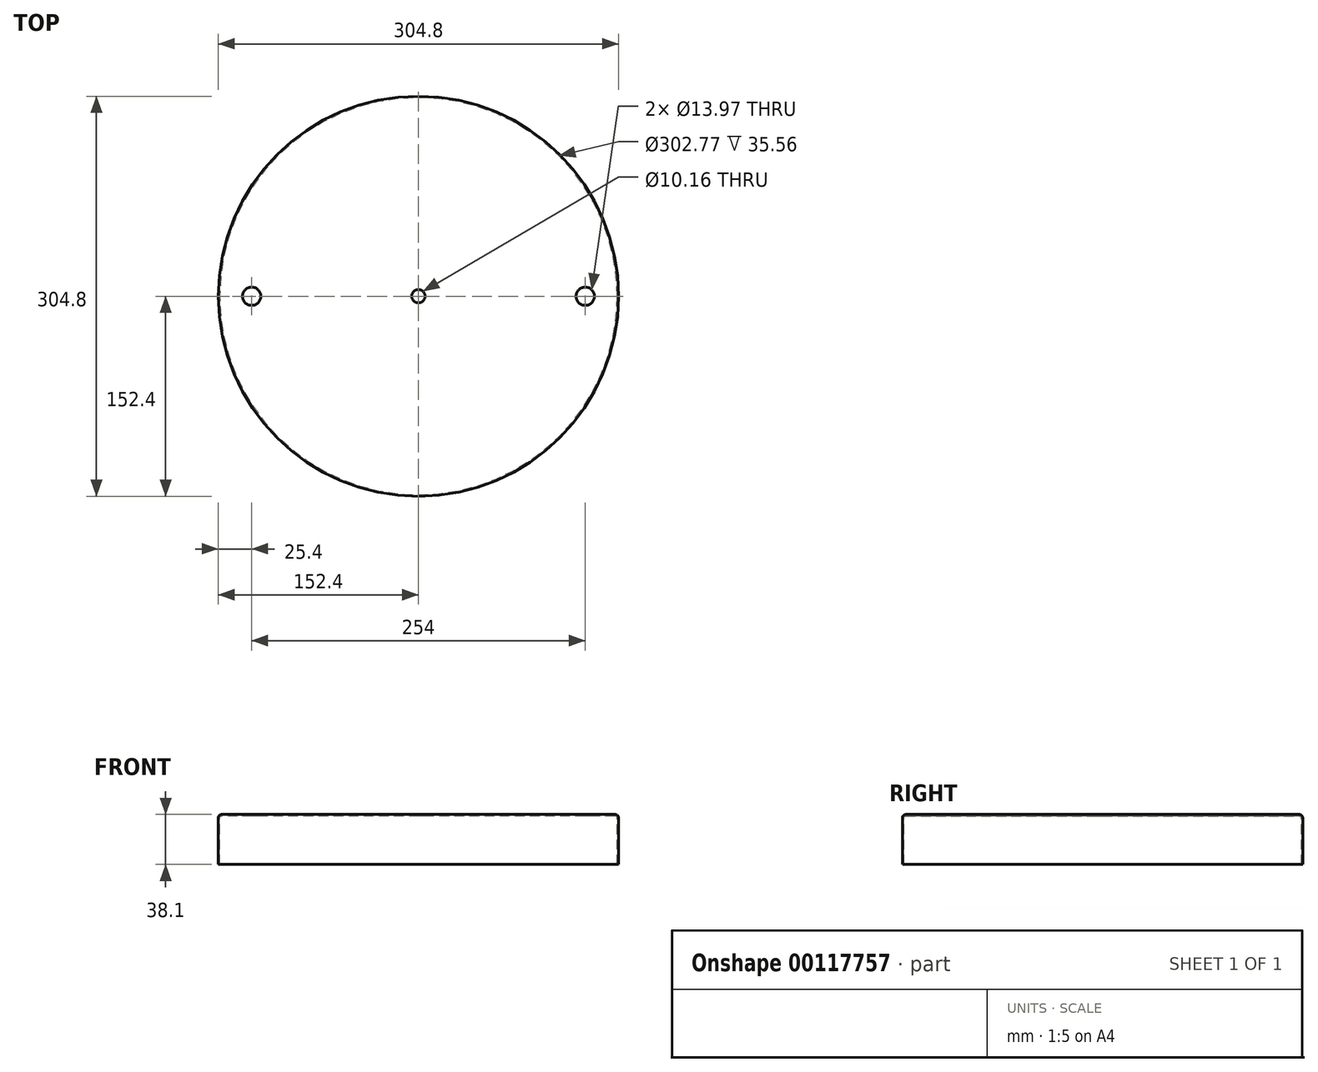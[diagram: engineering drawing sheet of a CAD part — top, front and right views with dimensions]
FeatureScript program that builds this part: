
annotation { "Feature Type Name" : "Feature", "Feature Type Description" : "" }
export const myFeature = defineFeature(function(context is Context, id is Id, definition is map)
    precondition{}
    {
        {
            var Q0;
            Q0=qCreatedBy(makeId("Top.planeOp"),FACE);
            var sketch = newSketch(context, id + "F0", { "sketchPlane" : qUnion([Q0])});
            skCircle(sketch, "E0", {"center": v(0, 0) * mm, "radius": 152.4 * mm, "construction": true});
            skCircle(sketch, "E1", {"center": v(127, 0) * mm, "radius": 6.99 * mm});
            skLineSegment(sketch, "E2", {"start": v(0, 0) * mm, "end": v(0, 88.23) * mm, "construction": true});
            skCircle(sketch, "E3.MirrorC", {"center": v(-127, 0) * mm, "radius": 6.99 * mm});
            skSolve(sketch);
        }
        {
            var Q0;
            Q0=qCreatedBy(makeId("Front.planeOp"),FACE);
            var sketch = newSketch(context, id + "F1", { "sketchPlane" : qUnion([Q0])});
            skLineSegment(sketch, "E4.0", {"start": v(-152.4, 0) * mm, "end": v(149.86, 0) * mm, "construction": true});
            skLineSegment(sketch, "E5", {"start": v(0, 0) * mm, "end": v(149.86, 0) * mm});
            skLineSegment(sketch, "E6", {"start": v(152.4, -2.54) * mm, "end": v(152.4, -38.1) * mm});
            skPoint(sketch, "E7.visualSharp", {"position": v(152.4, 0) * mm});
            skArc(sketch, "E7.filletArc", {"start": v(152.4, -2.54) * mm, "mid": v(151.66, -0.74) * mm, "end": v(149.86, 0) * mm});
            skLineSegment(sketch, "E8.0", {"start": v(151.38, -2.54) * mm, "end": v(151.38, -38.1) * mm});
            skArc(sketch, "E8.1", {"start": v(151.38, -2.54) * mm, "mid": v(150.94, -1.46) * mm, "end": v(149.86, -1.02) * mm});
            skLineSegment(sketch, "E8.2", {"start": v(0, -1.02) * mm, "end": v(149.86, -1.02) * mm});
            skLineSegment(sketch, "E9", {"start": v(152.4, -38.1) * mm, "end": v(151.38, -38.1) * mm});
            skLineSegment(sketch, "E10", {"start": v(0, -1.02) * mm, "end": v(0, 0) * mm});
            skLineSegment(sketch, "E11", {"start": v(0, -1.02) * mm, "end": v(0, -17.4) * mm, "construction": true});
            skSolve(sketch);
        }
        {
            var Q0;
            Q0 = qSketchRegion(id + "F1", true);
            var Q1;
            Q1=sQuery(id+"F1.wireOp",EDGE,"E11");
            revolve(context, id + "F2", {"entities" : qUnion([Q0]), "axis" : qUnion([Q1]), "revolveType" : RevolveType.FULL});
        }
        {
            var Q0;
            Q0=makeQuery(id+"F2.opRevolve","SWEPT_FACE",FACE,{"disambiguationData":[OSD([sQuery(id+"F1.wireOp",EDGE,"E5")])]});
            var sketch = newSketch(context, id + "F3", { "sketchPlane" : qUnion([Q0])});
            skCircle(sketch, "E12.0", {"center": v(0, 0) * mm, "radius": 152.4 * mm, "construction": true});
            skCircle(sketch, "E12.1", {"center": v(127, 0) * mm, "radius": 6.99 * mm});
            skLineSegment(sketch, "E12.2", {"start": v(0, 0) * mm, "end": v(0, 88.23) * mm, "construction": true});
            skCircle(sketch, "E12.3", {"center": v(-127, 0) * mm, "radius": 6.99 * mm});
            skCircle(sketch, "E13", {"center": v(0, 0) * mm, "radius": 5.08 * mm});
            skSolve(sketch);
        }
        {
            var Q0;
            Q0 = qSketchRegion(id + "F3", true);
            var Q1;
            Q1=makeQuery(id+"F2.opRevolve","SWEPT_FACE",FACE,{"disambiguationData":[OSD([sQuery(id+"F1.wireOp",EDGE,"E8.2")])]});
            extrude(context, id + "F4", {"entities" : qUnion([Q0]), "operationType" : NewBodyOperationType.REMOVE, "endBound" : BoundingType.UP_TO_SURFACE, "oppositeDirection" : true, "endBoundEntityFace" : qUnion([Q1]), "depth" : 25.4 * mm});
        }
    });
